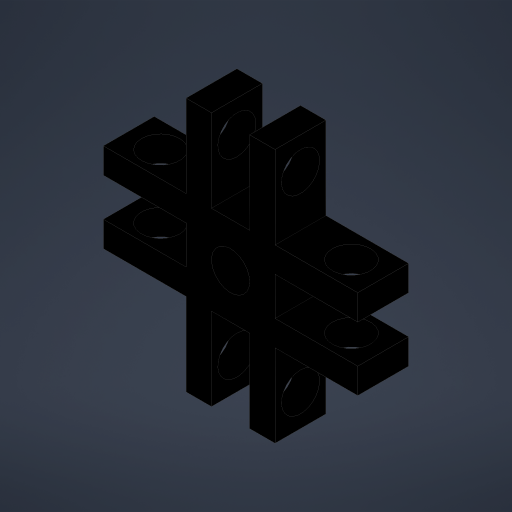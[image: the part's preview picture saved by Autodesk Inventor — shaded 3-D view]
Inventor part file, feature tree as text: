
AUTODESK INVENTOR PART (.ipt)
format: ipt  version: 2023 (Build 270158000, 158)  size: 249,344 bytes
history: native  units: mm
features: extrude x2, sketch x2, pattern_circular x1
ambient origin geometry x8: Origin, YZ Plane, XZ Plane, XY Plane, X Axis, Y Axis, Z Axis, Center Point
bodies: Solid1 (feature_tree)
feature tree (5):
  extrude  "Extrusion1"  Depth=20.0mm
  extrude  "Extrusion3"  Depth=2.0mm
  pattern_circular  "Circular Pattern2"  [2 undecoded]
  sketch  "Sketch1"  dims[d0=20.0mm d1=20.0mm]
  sketch  "Sketch3"  dims[d7=2.0mm d10=2.0mm d11=4.0mm d12=0.0mm d19=10.0mm d20=3.0mm d21=20.0mm d22=2.0mm d23=40.0mm d25=360.0deg d27=4.0mm d28=2.0mm d29=3.0mm d30=10.0mm d31=0.0mm d32=40.0mm d33=360.0deg]
note: 2 required parameter values undecoded (feature->parameter linkage not recoverable at this tier; creation-order binding heuristic only, values carry confidence <= 0.55)
